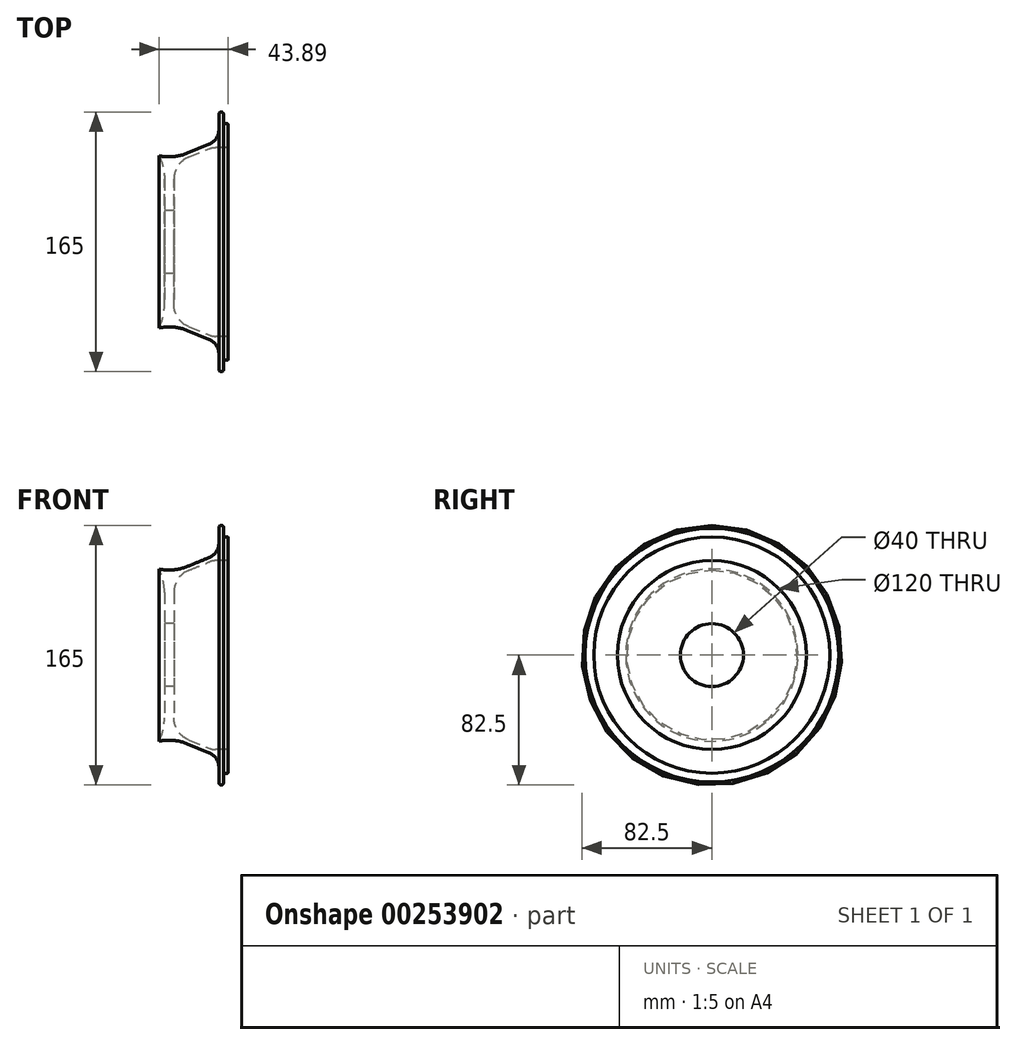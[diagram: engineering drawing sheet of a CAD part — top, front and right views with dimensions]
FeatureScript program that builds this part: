
annotation { "Feature Type Name" : "Feature", "Feature Type Description" : "" }
export const myFeature = defineFeature(function(context is Context, id is Id, definition is map)
    precondition{}
    {
        {
            var Q0;
            Q0=qCreatedBy(makeId("Front.planeOp"),FACE);
            var sketch = newSketch(context, id + "F0", { "sketchPlane" : qUnion([Q0])});
            skLineSegment(sketch, "E0", {"start": v(37.5, 75) * mm, "end": v(37.5, 60) * mm});
            skLineSegment(sketch, "E1", {"start": v(-37.5, 77.99) * mm, "end": v(-37.5, 81) * mm});
            skLineSegment(sketch, "E2", {"start": v(-32.8, 0) * mm, "end": v(49.68, 0) * mm, "construction": true});
            skLineSegment(sketch, "E3", {"start": v(-34.5, 81) * mm, "end": v(-34.5, 77.99) * mm});
            skLineSegment(sketch, "E4", {"start": v(34.5, 75) * mm, "end": v(37.5, 75) * mm});
            skLineSegment(sketch, "E5", {"start": v(34.5, 80.56) * mm, "end": v(34.5, 75) * mm});
            skLineSegment(sketch, "E6", {"start": v(29.46, 60) * mm, "end": v(37.5, 60) * mm});
            skLineSegment(sketch, "E7", {"start": v(3, 20) * mm, "end": v(3, 39.92) * mm});
            skLineSegment(sketch, "E8", {"start": v(12.33, 53.8) * mm, "end": v(25.68, 59.26) * mm});
            skPoint(sketch, "E9.orphan", {"position": v(37.5, 20) * mm});
            skLineSegment(sketch, "E10", {"start": v(0, -41.77) * mm, "end": v(0, 151.1) * mm, "construction": true});
            skPoint(sketch, "E11.visualSharp", {"position": v(3, 50) * mm});
            skArc(sketch, "E11.filletArc", {"start": v(12.33, 53.8) * mm, "mid": v(5.55, 48.29) * mm, "end": v(3, 39.92) * mm});
            skArc(sketch, "E12", {"start": v(-34.5, 81) * mm, "mid": v(-36, 82.5) * mm, "end": v(-37.5, 81) * mm});
            skPoint(sketch, "E12.third.point", {"position": v(-34.5, 81) * mm});
            skArc(sketch, "E13", {"start": v(34.5, 80.56) * mm, "mid": v(33.29, 82.48) * mm, "end": v(31.57, 81) * mm});
            skPoint(sketch, "E13.first.point", {"position": v(31.57, 81) * mm});
            skPoint(sketch, "E13.third.point", {"position": v(34.5, 80.56) * mm});
            skPoint(sketch, "E14.visualSharp", {"position": v(27.5, 60) * mm});
            skArc(sketch, "E14.filletArc", {"start": v(29.46, 60) * mm, "mid": v(27.54, 59.81) * mm, "end": v(25.68, 59.26) * mm});
            skLineSegment(sketch, "E15.1", {"start": v(0, 20) * mm, "end": v(0, 39.92) * mm});
            skLineSegment(sketch, "E16", {"start": v(31.57, 81) * mm, "end": v(31.57, 71.22) * mm});
            skPoint(sketch, "E17.third.point", {"position": v(13.53, 77.63) * mm});
            skLineSegment(sketch, "E18", {"start": v(11.34, 56.25) * mm, "end": v(25.34, 61.96) * mm});
            skArc(sketch, "E19.filletArc", {"start": v(25.34, 61.96) * mm, "mid": v(29.87, 65.64) * mm, "end": v(31.57, 71.22) * mm});
            skLineSegment(sketch, "E20", {"start": v(3, 20) * mm, "end": v(-3, 20) * mm});
            skPoint(sketch, "E21.visualSharp", {"position": v(-34.5, 74.99) * mm});
            skArc(sketch, "E21.filletArc", {"start": v(-34.5, 77.99) * mm, "mid": v(-33.71, 75.96) * mm, "end": v(-31.76, 75) * mm});
            skLineSegment(sketch, "E22.MirrorCS", {"start": v(-3, 20) * mm, "end": v(-3, 39.92) * mm});
            skArc(sketch, "E23", {"start": v(-11.34, 56.25) * mm, "mid": v(0, 54.02) * mm, "end": v(11.34, 56.25) * mm});
            skLineSegment(sketch, "E24", {"start": v(-31.76, 75) * mm, "end": v(-23.8, 74.3) * mm});
            skLineSegment(sketch, "E25.0", {"start": v(-32.02, 72.01) * mm, "end": v(-24.05, 71.31) * mm});
            skArc(sketch, "E25.1", {"start": v(-37.5, 77.99) * mm, "mid": v(-35.92, 73.94) * mm, "end": v(-32.02, 72.01) * mm});
            skArc(sketch, "E26", {"start": v(-3, 39.92) * mm, "mid": v(-8.75, 58.82) * mm, "end": v(-24.05, 71.31) * mm});
            skSolve(sketch);
        }
        {
            var Q0;
            Q0=makeQuery(id+"F0.imprint","IMPRINT",FACE,{"disambiguationData":[TD([[makeQuery(id+"F0.imprint","IMPRINT",EDGE,{"derivedFrom":sQuery(id+"F0.wireOp",EDGE,"vTGPbQuT-UWjS-oDgN-kqJf-HbyeZJuy5uQA")}),-1.0]])]});
            var Q1;
            Q1=makeQuery(id+"F0.imprint","IMPRINT",FACE,{"disambiguationData":[TD([[makeQuery(id+"F0.imprint","IMPRINT",EDGE,{"derivedFrom":sQuery(id+"F0.wireOp",EDGE,"E0")}),-1.0]])]});
            var Q2;
            Q2=sQuery(id+"F0.wireOp",EDGE,"E2");
            revolve(context, id + "F1", {"entities" : qUnion([Q0, Q1]), "axis" : qUnion([Q2]), "revolveType" : RevolveType.FULL});
        }
        {
            var Q0;
            Q0=makeQuery(id+"F1.opRevolve","SWEPT_EDGE",EDGE,{"disambiguationData":[OSD([sQuery(id+"F0.wireOp",EDGE,"E0"),sQuery(id+"F0.wireOp",EDGE,"E6")])]});
            var Q1;
            Q1=makeQuery(id+"F1.opRevolve","SWEPT_EDGE",EDGE,{"disambiguationData":[OSD([sQuery(id+"F0.wireOp",EDGE,"E0"),sQuery(id+"F0.wireOp",EDGE,"E4")])]});
            fillet(context, id + "F2", {"entities" : qUnion([Q0, Q1]), "radius" : .5 * mm, "tangentPropagation" : true, "allowEdgeOverflow" : false});
        }
    });
